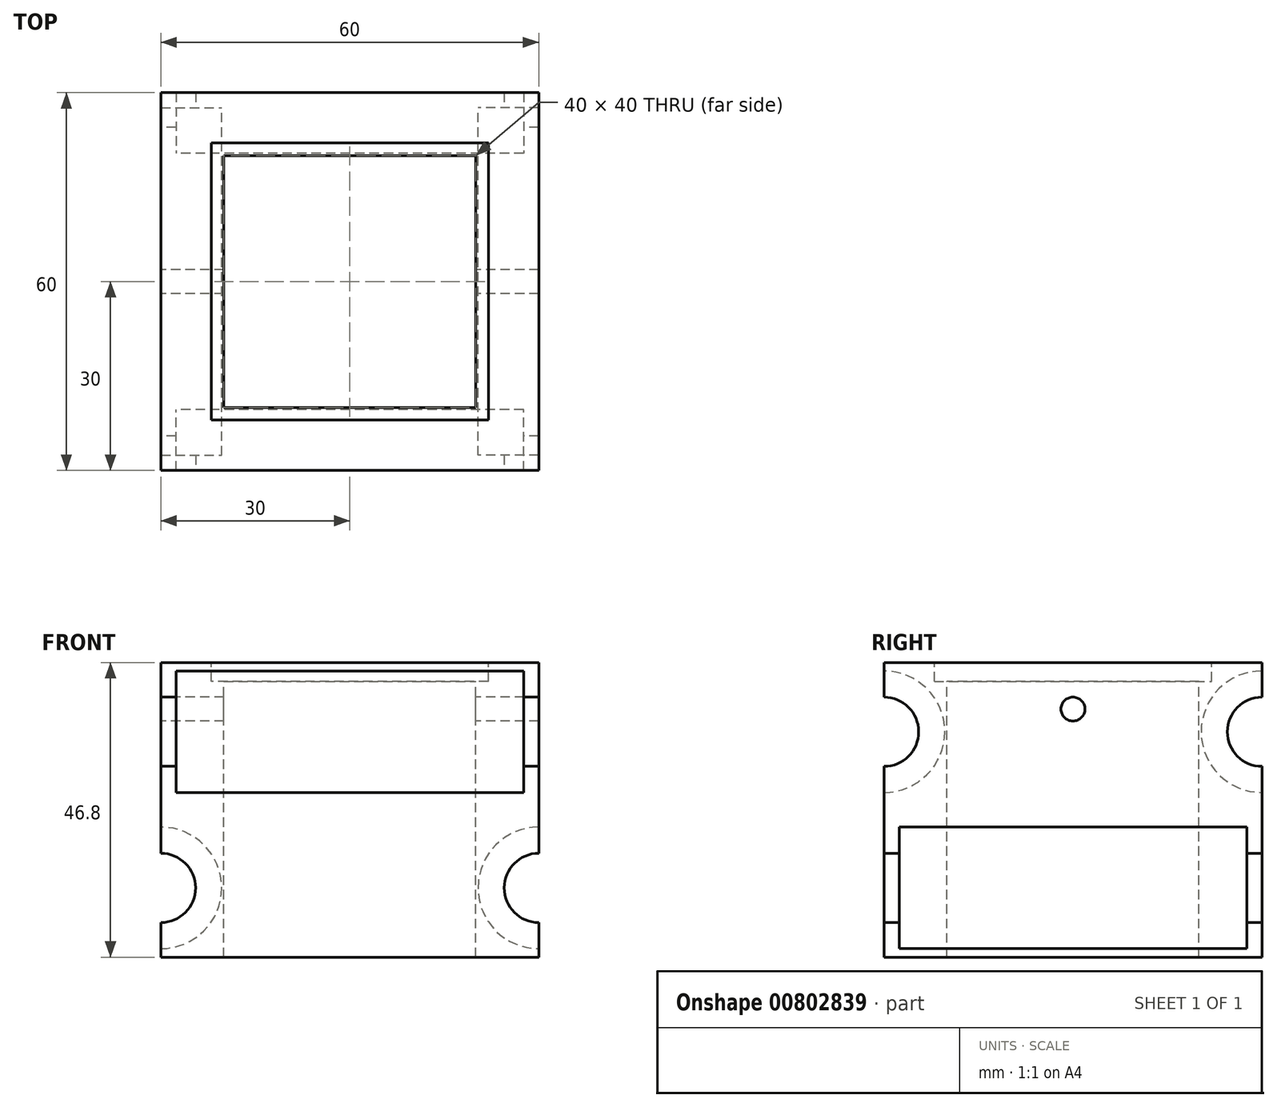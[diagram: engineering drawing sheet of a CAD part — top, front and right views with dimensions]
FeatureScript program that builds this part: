
annotation { "Feature Type Name" : "Feature", "Feature Type Description" : "" }
export const myFeature = defineFeature(function(context is Context, id is Id, definition is map)
    precondition{}
    {
        {
            var Q0;
            Q0=qCreatedBy(makeId("Top.planeOp"),FACE);
            var sketch = newSketch(context, id + "F0", { "sketchPlane" : qUnion([Q0])});
            skLineSegment(sketch, "E0.bottom", {"start": v(30, -30) * mm, "end": v(-30, -30) * mm});
            skLineSegment(sketch, "E0.top", {"start": v(30, 30) * mm, "end": v(-30, 30) * mm});
            skLineSegment(sketch, "E0.left", {"start": v(30, -30) * mm, "end": v(30, 30) * mm});
            skLineSegment(sketch, "E0.right", {"start": v(-30, -30) * mm, "end": v(-30, 30) * mm});
            skPoint(sketch, "E0.middle", {"position": v(0, 0) * mm});
            skSolve(sketch);
        }
        {
            var Q0;
            Q0=makeQuery(id+"F0.imprint","IMPRINT",FACE,{"disambiguationData":[TD([[makeQuery(id+"F0.imprint","IMPRINT",EDGE,{"derivedFrom":sQuery(id+"F0.wireOp",EDGE,"E0.bottom")}),-1.0]])]});
            extrude(context, id + "F1", {"entities" : qUnion([Q0]), "flatOperationType" : FlatOperationType.REMOVE, "depth" : 46.8 * mm, "offsetDistance" : 25 * mm, "domain" : OperationDomain.MODEL});
        }
        {
            var Q0;
            Q0=qCreatedBy(makeId("Right.planeOp"),FACE);
            var sketch = newSketch(context, id + "F2", { "sketchPlane" : qUnion([Q0])});
            skCircle(sketch, "E1", {"center": v(-30, 35.8) * mm, "radius": 9.65 * mm});
            skCircle(sketch, "E2", {"center": v(30, 35.8) * mm, "radius": 9.65 * mm});
            skSolve(sketch);
        }
        {
            var Q0;
            Q0 = qSketchRegion(id + "F2", true);
            extrude(context, id + "F3", {"entities" : qUnion([Q0]), "operationType" : NewBodyOperationType.REMOVE, "flatOperationType" : FlatOperationType.REMOVE, "depth" : 55.2 * mm, "offsetDistance" : 25 * mm, "domain" : OperationDomain.MODEL, "symmetric" : true});
        }
        {
            var Q0;
            Q0=qCreatedBy(makeId("Right.planeOp"),FACE);
            var sketch = newSketch(context, id + "F4", { "sketchPlane" : qUnion([Q0])});
            skCircle(sketch, "E3", {"center": v(-30, 35.8) * mm, "radius": 5.5 * mm});
            skCircle(sketch, "E4", {"center": v(30, 35.8) * mm, "radius": 5.5 * mm});
            skSolve(sketch);
        }
        {
            var Q0;
            Q0 = qSketchRegion(id + "F4", true);
            var Q1;
            Q1=sQuery(id+"F4.wireOp",EDGE,"E4");
            var Q2;
            Q2=sQuery(id+"F4.wireOp",EDGE,"E3");
            extrude(context, id + "F5", {"entities" : qUnion([Q0]), "operationType" : NewBodyOperationType.REMOVE, "surfaceEntities" : qUnion([Q1, Q2]), "depth" : 70 * mm, "offsetDistance" : 25 * mm, "symmetric" : true});
        }
        {
            var Q0;
            Q0=qCreatedBy(makeId("Front.planeOp"),FACE);
            var sketch = newSketch(context, id + "F6", { "sketchPlane" : qUnion([Q0])});
            skCircle(sketch, "E5", {"center": v(-30, 11) * mm, "radius": 9.65 * mm});
            skCircle(sketch, "E6", {"center": v(30, 11) * mm, "radius": 9.65 * mm});
            skSolve(sketch);
        }
        {
            var Q0;
            Q0=qCreatedBy(makeId("Front.planeOp"),FACE);
            var sketch = newSketch(context, id + "F7", { "sketchPlane" : qUnion([Q0])});
            skCircle(sketch, "E7", {"center": v(-30, 11) * mm, "radius": 5.5 * mm});
            skCircle(sketch, "E8", {"center": v(30, 11) * mm, "radius": 5.5 * mm});
            skSolve(sketch);
        }
        {
            var Q0;
            Q0 = qSketchRegion(id + "F7", true);
            extrude(context, id + "F8", {"entities" : qUnion([Q0]), "operationType" : NewBodyOperationType.REMOVE, "oppositeDirection" : true, "depth" : 75 * mm, "offsetDistance" : 25 * mm, "symmetric" : true});
        }
        {
            var Q0;
            Q0 = qSketchRegion(id + "F6", true);
            extrude(context, id + "F9", {"entities" : qUnion([Q0]), "operationType" : NewBodyOperationType.REMOVE, "flatOperationType" : FlatOperationType.REMOVE, "depth" : 55.2 * mm, "offsetDistance" : 25 * mm, "domain" : OperationDomain.MODEL, "symmetric" : true});
        }
        {
            var Q0;
            Q0=makeQuery(id+"F1.opExtrude","CAP_FACE",FACE,{"disambiguationData":[OSD([sQuery(id+"F0.wireOp",EDGE,"E0.bottom"),sQuery(id+"F0.wireOp",EDGE,"E0.top"),sQuery(id+"F0.wireOp",EDGE,"E0.left"),sQuery(id+"F0.wireOp",EDGE,"E0.right")])],"isStart":false});
            var sketch = newSketch(context, id + "F10", { "sketchPlane" : qUnion([Q0])});
            skLineSegment(sketch, "E9.bottom", {"start": v(20, -20) * mm, "end": v(-20, -20) * mm});
            skLineSegment(sketch, "E9.top", {"start": v(20, 20) * mm, "end": v(-20, 20) * mm});
            skLineSegment(sketch, "E9.left", {"start": v(20, -20) * mm, "end": v(20, 20) * mm});
            skLineSegment(sketch, "E9.right", {"start": v(-20, -20) * mm, "end": v(-20, 20) * mm});
            skPoint(sketch, "E9.middle", {"position": v(0, 0) * mm});
            skSolve(sketch);
        }
        {
            var Q0;
            Q0 = qSketchRegion(id + "F10", true);
            extrude(context, id + "F11", {"entities" : qUnion([Q0]), "operationType" : NewBodyOperationType.REMOVE, "flatOperationType" : FlatOperationType.REMOVE, "endBound" : BoundingType.THROUGH_ALL, "oppositeDirection" : true, "depth" : 45 * mm, "offsetDistance" : 25 * mm, "domain" : OperationDomain.MODEL});
        }
        {
            var Q0;
            Q0=makeQuery(id+"F1.opExtrude","CAP_FACE",FACE,{"disambiguationData":[OSD([sQuery(id+"F0.wireOp",EDGE,"E0.bottom"),sQuery(id+"F0.wireOp",EDGE,"E0.top"),sQuery(id+"F0.wireOp",EDGE,"E0.left"),sQuery(id+"F0.wireOp",EDGE,"E0.right")])],"isStart":false});
            var sketch = newSketch(context, id + "F12", { "sketchPlane" : qUnion([Q0])});
            skLineSegment(sketch, "E10.bottom", {"start": v(22, -22) * mm, "end": v(-22, -22) * mm});
            skLineSegment(sketch, "E10.top", {"start": v(22, 22) * mm, "end": v(-22, 22) * mm});
            skLineSegment(sketch, "E10.left", {"start": v(22, -22) * mm, "end": v(22, 22) * mm});
            skLineSegment(sketch, "E10.right", {"start": v(-22, -22) * mm, "end": v(-22, 22) * mm});
            skPoint(sketch, "E10.middle", {"position": v(0, 0) * mm});
            skSolve(sketch);
        }
        {
            var Q0;
            Q0 = qSketchRegion(id + "F12", true);
            extrude(context, id + "F13", {"entities" : qUnion([Q0]), "operationType" : NewBodyOperationType.REMOVE, "oppositeDirection" : true, "depth" : 3 * mm, "offsetDistance" : 25 * mm});
        }
        {
            var Q0;
            {var subQ2=sQuery(id+"F0.wireOp",EDGE,"E0.right");var subQ3=makeQuery(id+"F1.opExtrude","SWEPT_FACE",FACE,{"disambiguationData":[OSD([subQ2])]});Q0=makeQuery(id+"F8.boolean.opBoolean","SPLIT",FACE,{"disambiguationData":[TD([makeQuery(id+"F5.boolean.opBoolean","COPY",FACE,{"disambiguationData":[TD([subQ3])],"derivedFrom":makeQuery(id+"F5.opExtrude","SWEPT_FACE",FACE,{"disambiguationData":[OSD([sQuery(id+"F4.wireOp",EDGE,"E3")])]})})])],"derivedFrom":subQ3});}
            var sketch = newSketch(context, id + "F14", { "sketchPlane" : qUnion([Q0])});
            skCircle(sketch, "E11", {"center": v(0, 39.4) * mm, "radius": 1.9 * mm});
            skSolve(sketch);
        }
        {
            var Q0;
            Q0=makeQuery(id+"F14.imprint","IMPRINT",FACE,{"disambiguationData":[TD([[makeQuery(id+"F14.imprint","IMPRINT",EDGE,{"derivedFrom":sQuery(id+"F14.wireOp",EDGE,"E11")}),1.0]])]});
            extrude(context, id + "F15", {"entities" : qUnion([Q0]), "operationType" : NewBodyOperationType.REMOVE, "endBound" : BoundingType.THROUGH_ALL, "oppositeDirection" : true, "depth" : 100 * mm, "offsetDistance" : 25 * mm});
        }
    });
